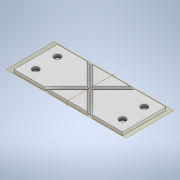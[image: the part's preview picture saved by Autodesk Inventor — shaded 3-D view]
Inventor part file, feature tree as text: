
AUTODESK INVENTOR PART (.ipt)
format: ipt  version: 2020 (Build 240168000, 168)  size: 216,576 bytes
history: native  units: mm
features: projected_geometry x6, extrude x3, sketch x3, plane x2, thicken_offset x2, chamfer x1, mirror x1
ambient origin geometry x8: Origin, YZ Plane, XZ Plane, XY Plane, X Axis, Y Axis, Z Axis, Center Point
bodies: Solid1 (feature_tree)
feature tree (18):
  extrude  "Extrusion1"  Depth=20.0mm
  plane  "Work Plane1"
  extrude  "Extrusion2"  Depth=10.0mm
  chamfer  "Chamfer1"  Distance=10.0mm
  extrude  "Extrusion3"  Depth=1.5mm
  plane  "Work Plane2"
  mirror  "Mirror1"
  thicken_offset  "Thicken1"
  thicken_offset  "Thicken2"
  sketch  "Sketch1"  dims[d0=50.0mm d1=20.0mm]
  sketch  "Sketch2"  dims[d2=10.0mm d3=10.0mm]
  projected_geometry  "Projected Loop1"
  projected_geometry  "Projected Loop2"
  projected_geometry  "Projected Loop3"
  projected_geometry  "Projected Loop4"
  sketch  "Sketch3"  dims[d4=10.0mm d5=10.0mm d6=0.5mm d7=40.0mm d8=0.5mm d9=40.0mm d10=1.5mm d11=0.0mm d12=0.15mm d13=0.0mm d14=0.675mm d15=2.0mm d16=45.0deg d17=5.0mm d18=5.0mm d19=5.0mm d20=3.0mm d21=3.0mm d22=4.0mm d23=0.0mm d24=0.07mm d25=0.07mm d26=0.07mm d27=0.07mm]
  projected_geometry  "Projected Loop5"
  projected_geometry  "Projected Loop6"
